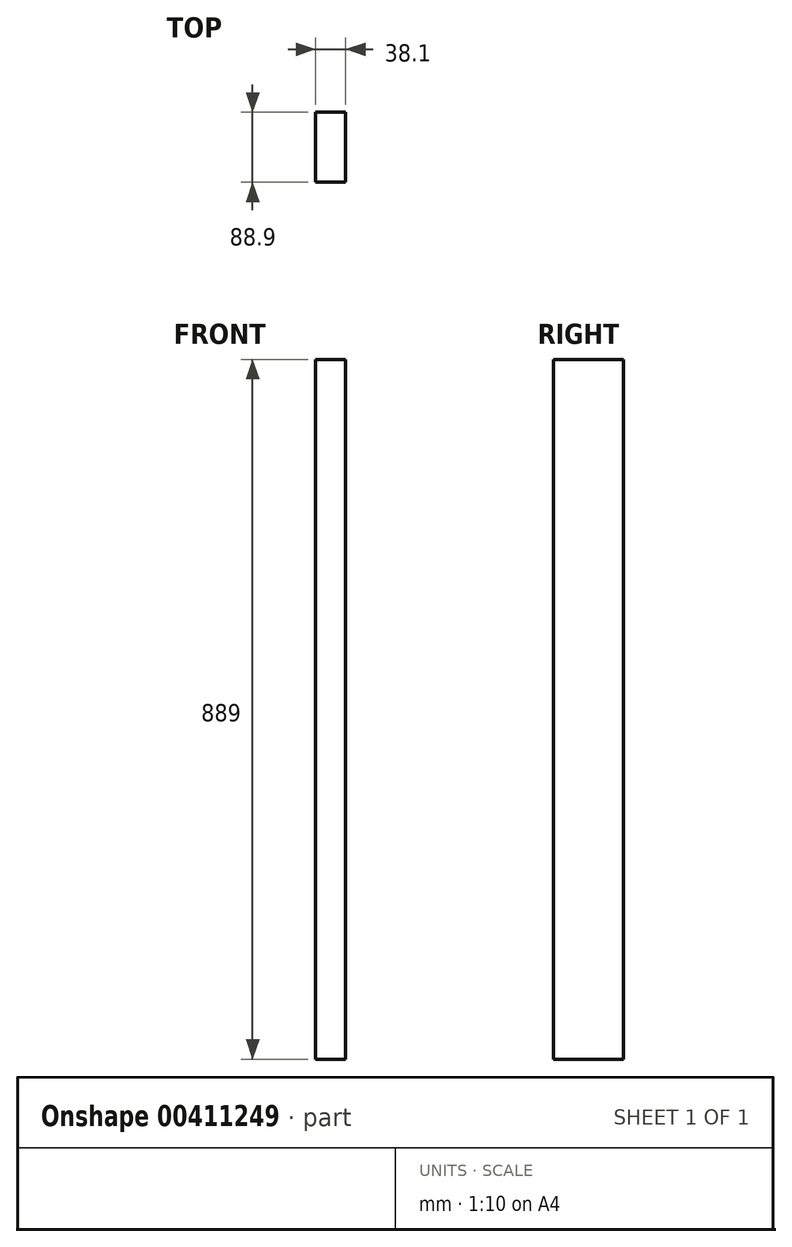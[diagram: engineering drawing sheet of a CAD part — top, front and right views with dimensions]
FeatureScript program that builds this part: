
annotation { "Feature Type Name" : "Feature", "Feature Type Description" : "" }
export const myFeature = defineFeature(function(context is Context, id is Id, definition is map)
    precondition{}
    {
        {
            var Q0;
            Q0=qCreatedBy(makeId("Top.planeOp"),FACE);
            var sketch = newSketch(context, id + "F0", { "sketchPlane" : qUnion([Q0])});
            skLineSegment(sketch, "E0.bottom", {"start": v(19.05, -44.45) * mm, "end": v(-19.05, -44.45) * mm});
            skLineSegment(sketch, "E0.top", {"start": v(19.05, 44.45) * mm, "end": v(-19.05, 44.45) * mm});
            skLineSegment(sketch, "E0.left", {"start": v(19.05, -44.45) * mm, "end": v(19.05, 44.45) * mm});
            skLineSegment(sketch, "E0.right", {"start": v(-19.05, -44.45) * mm, "end": v(-19.05, 44.45) * mm});
            skPoint(sketch, "E0.middle", {"position": v(0, 0) * mm});
            skSolve(sketch);
        }
        {
            var Q0;
            Q0=makeQuery(id+"F0.imprint","IMPRINT",FACE,{"disambiguationData":[TD([[makeQuery(id+"F0.imprint","IMPRINT",EDGE,{"derivedFrom":sQuery(id+"F0.wireOp",EDGE,"E0.bottom")}),-1.0]])]});
            extrude(context, id + "F1", {"entities" : qUnion([Q0]), "depth" : 889 * mm});
        }
    });
